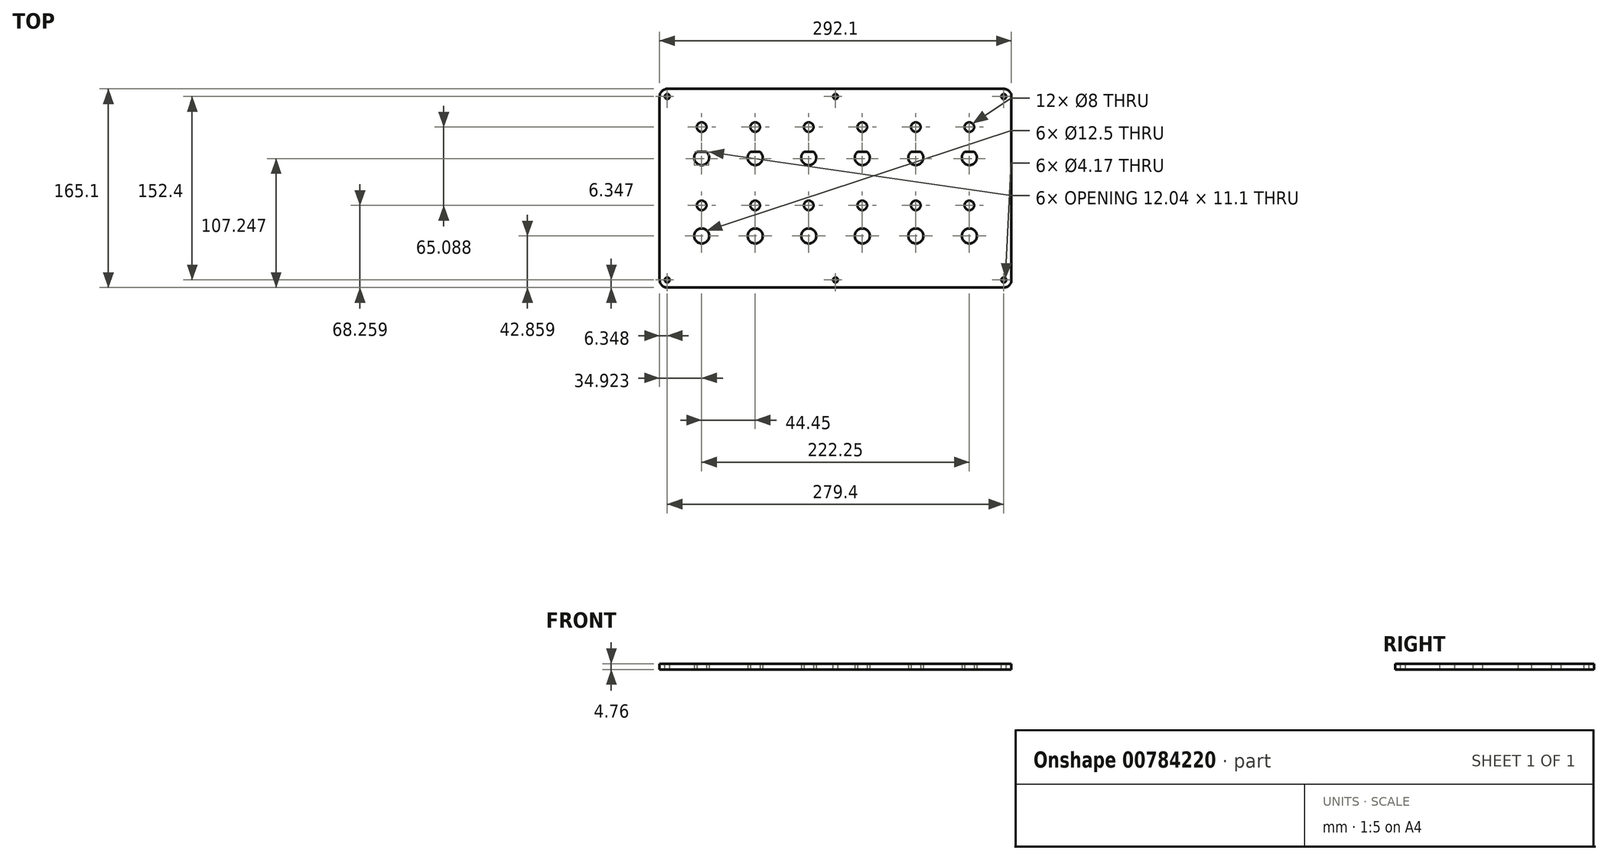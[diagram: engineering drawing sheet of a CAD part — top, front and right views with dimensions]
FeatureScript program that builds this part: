
annotation { "Feature Type Name" : "Feature", "Feature Type Description" : "" }
export const myFeature = defineFeature(function(context is Context, id is Id, definition is map)
    precondition{}
    {
        {
            var Q0;
            Q0=qCreatedBy(makeId("Top.planeOp"),FACE);
            var sketch = newSketch(context, id + "F0", { "sketchPlane" : qUnion([Q0])});
            skPoint(sketch, "E0", {"position": v(-87.04, 42.22) * mm});
            skPoint(sketch, "E1", {"position": v(-87.04, 16.82) * mm});
            skCircle(sketch, "E2", {"center": v(-87.04, 16.82) * mm, "radius": 6.25 * mm});
            skLineSegment(sketch, "E3", {"start": v(-90.98, 21.67) * mm, "end": v(-83.1, 21.67) * mm});
            skPoint(sketch, "E4.0.1.0", {"position": v(-87.04, -48.27) * mm});
            skPoint(sketch, "E4.0.1.1", {"position": v(-87.04, -22.87) * mm});
            skCircle(sketch, "E4.0.1.2", {"center": v(-87.04, -48.27) * mm, "radius": 6.25 * mm});
            skPoint(sketch, "E4.1.0.0", {"position": v(-42.59, 16.82) * mm});
            skPoint(sketch, "E4.1.0.1", {"position": v(-42.59, 42.22) * mm});
            skCircle(sketch, "E4.1.0.2", {"center": v(-42.59, 16.82) * mm, "radius": 6.25 * mm});
            skLineSegment(sketch, "E4.1.0.3", {"start": v(-46.53, 21.67) * mm, "end": v(-38.65, 21.67) * mm});
            skPoint(sketch, "E4.1.1.0", {"position": v(-42.59, -48.27) * mm});
            skPoint(sketch, "E4.1.1.1", {"position": v(-42.59, -22.87) * mm});
            skCircle(sketch, "E4.1.1.2", {"center": v(-42.59, -48.27) * mm, "radius": 6.25 * mm});
            skPoint(sketch, "E4.2.0.0", {"position": v(1.86, 16.82) * mm});
            skPoint(sketch, "E4.2.0.1", {"position": v(1.86, 42.22) * mm});
            skCircle(sketch, "E4.2.0.2", {"center": v(1.86, 16.82) * mm, "radius": 6.25 * mm});
            skLineSegment(sketch, "E4.2.0.3", {"start": v(-2.08, 21.67) * mm, "end": v(5.8, 21.67) * mm});
            skPoint(sketch, "E4.2.1.0", {"position": v(1.86, -48.27) * mm});
            skPoint(sketch, "E4.2.1.1", {"position": v(1.86, -22.87) * mm});
            skCircle(sketch, "E4.2.1.2", {"center": v(1.86, -48.27) * mm, "radius": 6.25 * mm});
            skPoint(sketch, "E4.3.0.0", {"position": v(46.31, 16.82) * mm});
            skPoint(sketch, "E4.3.0.1", {"position": v(46.31, 42.22) * mm});
            skCircle(sketch, "E4.3.0.2", {"center": v(46.31, 16.82) * mm, "radius": 6.25 * mm});
            skLineSegment(sketch, "E4.3.0.3", {"start": v(42.37, 21.67) * mm, "end": v(50.25, 21.67) * mm});
            skPoint(sketch, "E4.3.1.0", {"position": v(46.31, -48.27) * mm});
            skPoint(sketch, "E4.3.1.1", {"position": v(46.31, -22.87) * mm});
            skCircle(sketch, "E4.3.1.2", {"center": v(46.31, -48.27) * mm, "radius": 6.25 * mm});
            skPoint(sketch, "E4.4.0.0", {"position": v(90.76, 16.82) * mm});
            skPoint(sketch, "E4.4.0.1", {"position": v(90.76, 42.22) * mm});
            skCircle(sketch, "E4.4.0.2", {"center": v(90.76, 16.82) * mm, "radius": 6.25 * mm});
            skLineSegment(sketch, "E4.4.0.3", {"start": v(86.82, 21.67) * mm, "end": v(94.7, 21.67) * mm});
            skPoint(sketch, "E4.4.1.0", {"position": v(90.76, -48.27) * mm});
            skPoint(sketch, "E4.4.1.1", {"position": v(90.76, -22.87) * mm});
            skCircle(sketch, "E4.4.1.2", {"center": v(90.76, -48.27) * mm, "radius": 6.25 * mm});
            skPoint(sketch, "E4.5.0.0", {"position": v(135.21, 16.82) * mm});
            skPoint(sketch, "E4.5.0.1", {"position": v(135.21, 42.22) * mm});
            skCircle(sketch, "E4.5.0.2", {"center": v(135.21, 16.82) * mm, "radius": 6.25 * mm});
            skLineSegment(sketch, "E4.5.0.3", {"start": v(131.27, 21.67) * mm, "end": v(139.15, 21.67) * mm});
            skPoint(sketch, "E4.5.1.0", {"position": v(135.21, -48.27) * mm});
            skPoint(sketch, "E4.5.1.1", {"position": v(135.21, -22.87) * mm});
            skCircle(sketch, "E4.5.1.2", {"center": v(135.21, -48.27) * mm, "radius": 6.25 * mm});
            skLineSegment(sketch, "E4.direction1", {"start": v(-87.04, 16.82) * mm, "end": v(-42.59, 16.82) * mm, "construction": true});
            skLineSegment(sketch, "E4.direction2", {"start": v(-87.04, 16.82) * mm, "end": v(-87.04, -48.27) * mm, "construction": true});
            skLineSegment(sketch, "E5.bottom", {"start": v(-115.61, 73.97) * mm, "end": v(163.79, 73.97) * mm});
            skLineSegment(sketch, "E5.top", {"start": v(-115.61, -91.13) * mm, "end": v(163.79, -91.13) * mm});
            skLineSegment(sketch, "E5.left", {"start": v(-121.96, 67.62) * mm, "end": v(-121.96, -84.78) * mm});
            skLineSegment(sketch, "E5.right", {"start": v(170.14, 67.62) * mm, "end": v(170.14, -84.78) * mm});
            skPoint(sketch, "E6.visualSharp", {"position": v(-121.96, 73.97) * mm});
            skArc(sketch, "E6.filletArc", {"start": v(-115.61, 73.97) * mm, "mid": v(-120.1, 72.1) * mm, "end": v(-121.96, 67.62) * mm});
            skPoint(sketch, "E7.visualSharp", {"position": v(-121.96, -91.13) * mm});
            skArc(sketch, "E7.filletArc", {"start": v(-121.96, -84.78) * mm, "mid": v(-120.1, -89.27) * mm, "end": v(-115.61, -91.13) * mm});
            skPoint(sketch, "E8.visualSharp", {"position": v(170.14, -91.13) * mm});
            skArc(sketch, "E8.filletArc", {"start": v(163.79, -91.13) * mm, "mid": v(168.28, -89.27) * mm, "end": v(170.14, -84.78) * mm});
            skPoint(sketch, "E9.visualSharp", {"position": v(170.14, 73.97) * mm});
            skArc(sketch, "E9.filletArc", {"start": v(170.14, 67.62) * mm, "mid": v(168.28, 72.1) * mm, "end": v(163.79, 73.97) * mm});
            skSolve(sketch);
        }
        {
            var Q0;
            Q0=makeQuery(id+"F0.imprint","IMPRINT",FACE,{"disambiguationData":[TD([[makeQuery(id+"F0.imprint","IMPRINT",EDGE,{"derivedFrom":sQuery(id+"F0.wireOp",EDGE,"E5.bottom")}),-1.0]])]});
            var Q1;
            {var subQ0=sQuery(id+"F0.wireOp",EDGE,"E4.1.0.3");Q1=makeQuery(id+"F0.imprint","IMPRINT",FACE,{"disambiguationData":[TD([[makeQuery(id+"F0.imprint","IMPRINT",EDGE,{"derivedFrom":subQ0}),1.0]])]});}
            var Q2;
            {var subQ0=sQuery(id+"F0.wireOp",EDGE,"E3");Q2=makeQuery(id+"F0.imprint","IMPRINT",FACE,{"disambiguationData":[TD([[makeQuery(id+"F0.imprint","IMPRINT",EDGE,{"derivedFrom":subQ0}),1.0]])]});}
            var Q3;
            {var subQ0=sQuery(id+"F0.wireOp",EDGE,"E4.5.0.3");Q3=makeQuery(id+"F0.imprint","IMPRINT",FACE,{"disambiguationData":[TD([[makeQuery(id+"F0.imprint","IMPRINT",EDGE,{"derivedFrom":subQ0}),1.0]])]});}
            var Q4;
            {var subQ0=sQuery(id+"F0.wireOp",EDGE,"E4.3.0.3");Q4=makeQuery(id+"F0.imprint","IMPRINT",FACE,{"disambiguationData":[TD([[makeQuery(id+"F0.imprint","IMPRINT",EDGE,{"derivedFrom":subQ0}),1.0]])]});}
            var Q5;
            {var subQ0=sQuery(id+"F0.wireOp",EDGE,"E4.2.0.3");Q5=makeQuery(id+"F0.imprint","IMPRINT",FACE,{"disambiguationData":[TD([[makeQuery(id+"F0.imprint","IMPRINT",EDGE,{"derivedFrom":subQ0}),1.0]])]});}
            var Q6;
            {var subQ0=sQuery(id+"F0.wireOp",EDGE,"E4.4.0.3");Q6=makeQuery(id+"F0.imprint","IMPRINT",FACE,{"disambiguationData":[TD([[makeQuery(id+"F0.imprint","IMPRINT",EDGE,{"derivedFrom":subQ0}),1.0]])]});}
            var Q7;
            {var subQ0=sQuery(id+"F0.wireOp",EDGE,"E4.2.1.3");Q7=makeQuery(id+"F0.imprint","IMPRINT",FACE,{"disambiguationData":[TD([[makeQuery(id+"F0.imprint","IMPRINT",EDGE,{"derivedFrom":subQ0}),1.0]])]});}
            var Q8;
            {var subQ0=sQuery(id+"F0.wireOp",EDGE,"E4.3.1.3");Q8=makeQuery(id+"F0.imprint","IMPRINT",FACE,{"disambiguationData":[TD([[makeQuery(id+"F0.imprint","IMPRINT",EDGE,{"derivedFrom":subQ0}),1.0]])]});}
            var Q9;
            {var subQ0=sQuery(id+"F0.wireOp",EDGE,"E4.4.1.3");Q9=makeQuery(id+"F0.imprint","IMPRINT",FACE,{"disambiguationData":[TD([[makeQuery(id+"F0.imprint","IMPRINT",EDGE,{"derivedFrom":subQ0}),1.0]])]});}
            var Q10;
            {var subQ0=sQuery(id+"F0.wireOp",EDGE,"E4.1.1.3");Q10=makeQuery(id+"F0.imprint","IMPRINT",FACE,{"disambiguationData":[TD([[makeQuery(id+"F0.imprint","IMPRINT",EDGE,{"derivedFrom":subQ0}),1.0]])]});}
            var Q11;
            {var subQ0=sQuery(id+"F0.wireOp",EDGE,"E4.0.1.3");Q11=makeQuery(id+"F0.imprint","IMPRINT",FACE,{"disambiguationData":[TD([[makeQuery(id+"F0.imprint","IMPRINT",EDGE,{"derivedFrom":subQ0}),1.0]])]});}
            var Q12;
            {var subQ0=sQuery(id+"F0.wireOp",EDGE,"E4.5.1.3");Q12=makeQuery(id+"F0.imprint","IMPRINT",FACE,{"disambiguationData":[TD([[makeQuery(id+"F0.imprint","IMPRINT",EDGE,{"derivedFrom":subQ0}),1.0]])]});}
            extrude(context, id + "F1", {"entities" : qUnion([Q0, Q1, Q2, Q3, Q4, Q5, Q6, Q7, Q8, Q9, Q10, Q11, Q12]), "depth" : 4.76 * mm, "offsetDistance" : 25.4 * mm});
        }
        {
            var Q0;
            Q0=sQuery(id+"F0.wireOp",VERTEX,"E4.3.0.1");
            var Q1;
            Q1=sQuery(id+"F0.wireOp",VERTEX,"E4.5.0.1");
            var Q2;
            Q2=sQuery(id+"F0.wireOp",VERTEX,"E0");
            var Q3;
            Q3=sQuery(id+"F0.wireOp",VERTEX,"E4.1.0.1");
            var Q4;
            Q4=sQuery(id+"F0.wireOp",VERTEX,"E4.2.0.1");
            var Q5;
            Q5=sQuery(id+"F0.wireOp",VERTEX,"E4.4.0.1");
            var Q6;
            Q6=sQuery(id+"F0.wireOp",VERTEX,"E4.2.1.1");
            var Q7;
            Q7=sQuery(id+"F0.wireOp",VERTEX,"E4.0.1.1");
            var Q8;
            Q8=sQuery(id+"F0.wireOp",VERTEX,"E4.4.1.1");
            var Q9;
            Q9=sQuery(id+"F0.wireOp",VERTEX,"E4.1.1.1");
            var Q10;
            Q10=sQuery(id+"F0.wireOp",VERTEX,"E4.5.1.1");
            var Q11;
            Q11=sQuery(id+"F0.wireOp",VERTEX,"E4.3.1.1");
            var Q12;
            Q12=makeQuery(id+"F1.opExtrude","SWEPT_BODY",BODY,{"disambiguationData":[OSD([sQuery(id+"F0.wireOp",EDGE,"E2"),sQuery(id+"F0.wireOp",EDGE,"E3"),sQuery(id+"F0.wireOp",EDGE,"E4.0.1.2"),sQuery(id+"F0.wireOp",EDGE,"E4.0.1.3"),sQuery(id+"F0.wireOp",EDGE,"E4.1.0.2"),sQuery(id+"F0.wireOp",EDGE,"E4.1.0.3"),sQuery(id+"F0.wireOp",EDGE,"E4.1.1.2"),sQuery(id+"F0.wireOp",EDGE,"E4.1.1.3"),sQuery(id+"F0.wireOp",EDGE,"E4.2.0.2"),sQuery(id+"F0.wireOp",EDGE,"E4.2.0.3"),sQuery(id+"F0.wireOp",EDGE,"E4.2.1.2"),sQuery(id+"F0.wireOp",EDGE,"E4.2.1.3"),sQuery(id+"F0.wireOp",EDGE,"E4.3.0.2"),sQuery(id+"F0.wireOp",EDGE,"E4.3.0.3"),sQuery(id+"F0.wireOp",EDGE,"E4.3.1.2"),sQuery(id+"F0.wireOp",EDGE,"E4.3.1.3"),sQuery(id+"F0.wireOp",EDGE,"E4.4.0.2"),sQuery(id+"F0.wireOp",EDGE,"E4.4.0.3"),sQuery(id+"F0.wireOp",EDGE,"E4.4.1.2"),sQuery(id+"F0.wireOp",EDGE,"E4.4.1.3"),sQuery(id+"F0.wireOp",EDGE,"E4.5.0.2"),sQuery(id+"F0.wireOp",EDGE,"E4.5.0.3"),sQuery(id+"F0.wireOp",EDGE,"E4.5.1.2"),sQuery(id+"F0.wireOp",EDGE,"E4.5.1.3"),sQuery(id+"F0.wireOp",EDGE,"E5.bottom"),sQuery(id+"F0.wireOp",EDGE,"E5.top"),sQuery(id+"F0.wireOp",EDGE,"E5.left"),sQuery(id+"F0.wireOp",EDGE,"E5.right")])]});
            hole(context, id + "F2", {"style" : HoleStyle.SIMPLE, "endStyle" : HoleEndStyle.THROUGH, "oppositeDirection" : true, "holeDiameter" : 8 * mm, "majorDiameter" : 6.35 * mm, "isTappedThrough" : true, "tappedDepth" : 12.7 * mm, "tapClearance" : 3, "locations" : qUnion([Q0, Q1, Q2, Q3, Q4, Q5, Q6, Q7, Q8, Q9, Q10, Q11]), "scope" : qUnion([Q12])});
        }
        {
            var Q0;
            Q0=makeQuery(id+"F1.opExtrude","CAP_FACE",FACE,{"disambiguationData":[OSD([sQuery(id+"F0.wireOp",EDGE,"E2"),sQuery(id+"F0.wireOp",EDGE,"E3"),sQuery(id+"F0.wireOp",EDGE,"E4.0.1.2"),sQuery(id+"F0.wireOp",EDGE,"E4.0.1.3"),sQuery(id+"F0.wireOp",EDGE,"E4.1.0.2"),sQuery(id+"F0.wireOp",EDGE,"E4.1.0.3"),sQuery(id+"F0.wireOp",EDGE,"E4.1.1.2"),sQuery(id+"F0.wireOp",EDGE,"E4.1.1.3"),sQuery(id+"F0.wireOp",EDGE,"E4.2.0.2"),sQuery(id+"F0.wireOp",EDGE,"E4.2.0.3"),sQuery(id+"F0.wireOp",EDGE,"E4.2.1.2"),sQuery(id+"F0.wireOp",EDGE,"E4.2.1.3"),sQuery(id+"F0.wireOp",EDGE,"E4.3.0.2"),sQuery(id+"F0.wireOp",EDGE,"E4.3.0.3"),sQuery(id+"F0.wireOp",EDGE,"E4.3.1.2"),sQuery(id+"F0.wireOp",EDGE,"E4.3.1.3"),sQuery(id+"F0.wireOp",EDGE,"E4.4.0.2"),sQuery(id+"F0.wireOp",EDGE,"E4.4.0.3"),sQuery(id+"F0.wireOp",EDGE,"E4.4.1.2"),sQuery(id+"F0.wireOp",EDGE,"E4.4.1.3"),sQuery(id+"F0.wireOp",EDGE,"E4.5.0.2"),sQuery(id+"F0.wireOp",EDGE,"E4.5.0.3"),sQuery(id+"F0.wireOp",EDGE,"E4.5.1.2"),sQuery(id+"F0.wireOp",EDGE,"E4.5.1.3"),sQuery(id+"F0.wireOp",EDGE,"E5.bottom"),sQuery(id+"F0.wireOp",EDGE,"E5.top"),sQuery(id+"F0.wireOp",EDGE,"E5.left"),sQuery(id+"F0.wireOp",EDGE,"E5.right")])],"isStart":false});
            var sketch = newSketch(context, id + "F3", { "sketchPlane" : qUnion([Q0])});
            skPoint(sketch, "E10", {"position": v(-115.61, 67.62) * mm});
            skPoint(sketch, "E11", {"position": v(-115.61, -84.78) * mm});
            skPoint(sketch, "E12", {"position": v(163.79, -84.78) * mm});
            skPoint(sketch, "E13", {"position": v(163.79, 67.62) * mm});
            skPoint(sketch, "E14", {"position": v(24.09, 67.62) * mm});
            skPoint(sketch, "E15", {"position": v(24.09, -84.78) * mm});
            skSolve(sketch);
        }
        {
            var Q0;
            Q0=sQuery(id+"F3.wireOp",VERTEX,"E10");
            var Q1;
            Q1=sQuery(id+"F3.wireOp",VERTEX,"E13");
            var Q2;
            Q2=sQuery(id+"F3.wireOp",VERTEX,"E12");
            var Q3;
            Q3=sQuery(id+"F3.wireOp",VERTEX,"E11");
            var Q4;
            Q4=sQuery(id+"F3.wireOp",VERTEX,"E14");
            var Q5;
            Q5=sQuery(id+"F3.wireOp",VERTEX,"E15");
            var Q6;
            Q6=makeQuery(id+"F1.opExtrude","SWEPT_BODY",BODY,{"disambiguationData":[OSD([sQuery(id+"F0.wireOp",EDGE,"E2"),sQuery(id+"F0.wireOp",EDGE,"E3"),sQuery(id+"F0.wireOp",EDGE,"E4.0.1.2"),sQuery(id+"F0.wireOp",EDGE,"E4.0.1.3"),sQuery(id+"F0.wireOp",EDGE,"E4.1.0.2"),sQuery(id+"F0.wireOp",EDGE,"E4.1.0.3"),sQuery(id+"F0.wireOp",EDGE,"E4.1.1.2"),sQuery(id+"F0.wireOp",EDGE,"E4.1.1.3"),sQuery(id+"F0.wireOp",EDGE,"E4.2.0.2"),sQuery(id+"F0.wireOp",EDGE,"E4.2.0.3"),sQuery(id+"F0.wireOp",EDGE,"E4.2.1.2"),sQuery(id+"F0.wireOp",EDGE,"E4.2.1.3"),sQuery(id+"F0.wireOp",EDGE,"E4.3.0.2"),sQuery(id+"F0.wireOp",EDGE,"E4.3.0.3"),sQuery(id+"F0.wireOp",EDGE,"E4.3.1.2"),sQuery(id+"F0.wireOp",EDGE,"E4.3.1.3"),sQuery(id+"F0.wireOp",EDGE,"E4.4.0.2"),sQuery(id+"F0.wireOp",EDGE,"E4.4.0.3"),sQuery(id+"F0.wireOp",EDGE,"E4.4.1.2"),sQuery(id+"F0.wireOp",EDGE,"E4.4.1.3"),sQuery(id+"F0.wireOp",EDGE,"E4.5.0.2"),sQuery(id+"F0.wireOp",EDGE,"E4.5.0.3"),sQuery(id+"F0.wireOp",EDGE,"E4.5.1.2"),sQuery(id+"F0.wireOp",EDGE,"E4.5.1.3"),sQuery(id+"F0.wireOp",EDGE,"E5.bottom"),sQuery(id+"F0.wireOp",EDGE,"E5.top"),sQuery(id+"F0.wireOp",EDGE,"E5.left"),sQuery(id+"F0.wireOp",EDGE,"E5.right")])]});
            hole(context, id + "F4", {"style" : HoleStyle.SIMPLE, "endStyle" : HoleEndStyle.THROUGH, "holeDiameter" : 4.17 * mm, "majorDiameter" : 6.35 * mm, "isTappedThrough" : true, "tappedDepth" : 12.7 * mm, "tapClearance" : 3, "locations" : qUnion([Q0, Q1, Q2, Q3, Q4, Q5]), "scope" : qUnion([Q6])});
        }
    });
